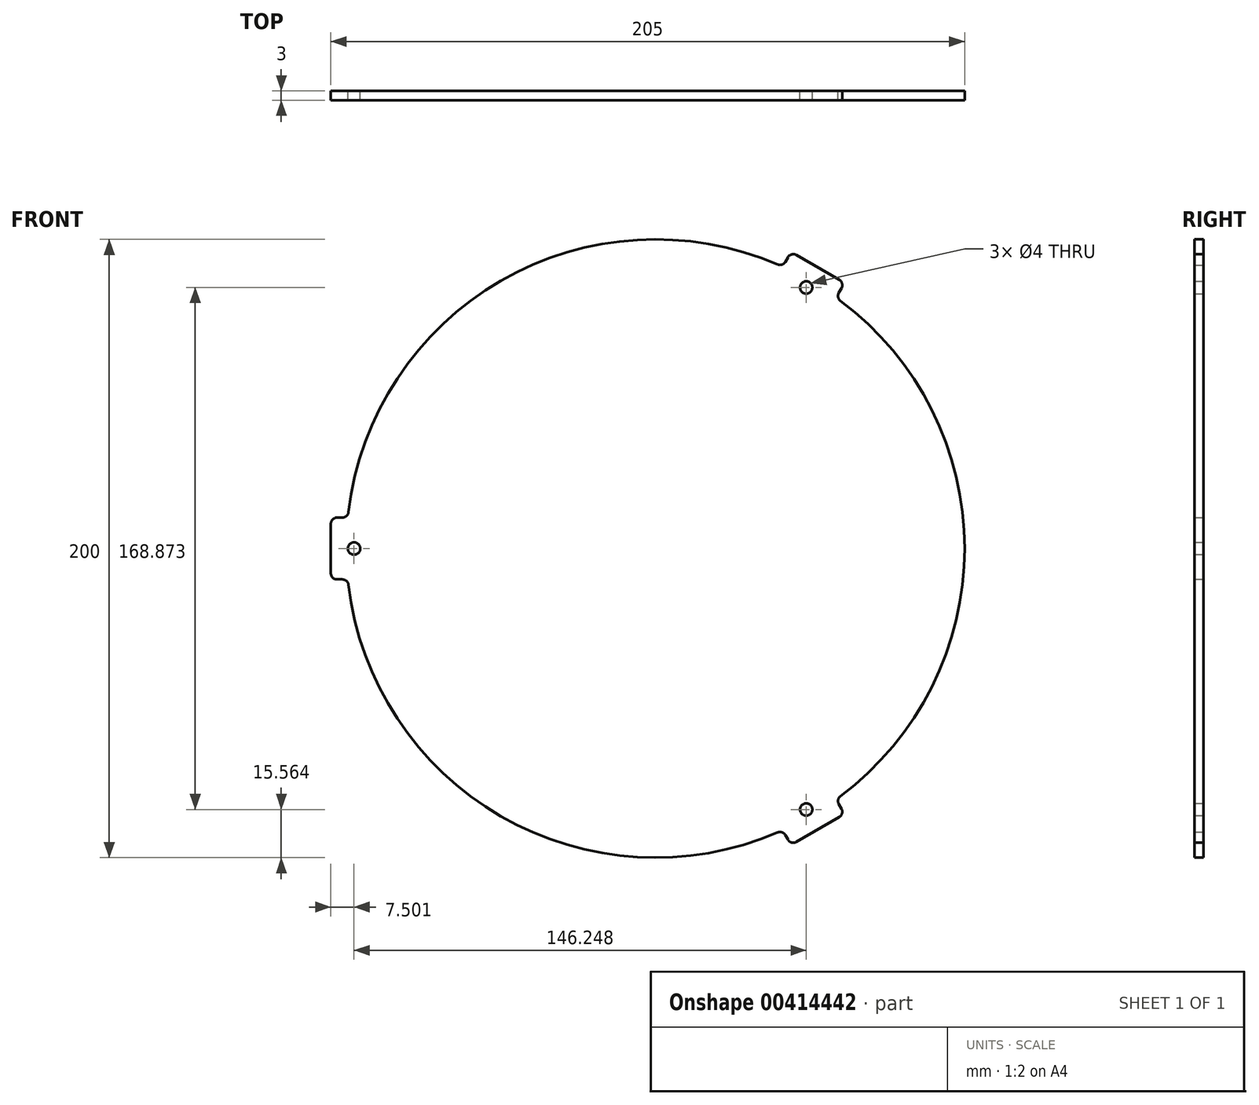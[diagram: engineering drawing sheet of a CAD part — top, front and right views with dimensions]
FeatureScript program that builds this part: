
annotation { "Feature Type Name" : "Feature", "Feature Type Description" : "" }
export const myFeature = defineFeature(function(context is Context, id is Id, definition is map)
    precondition{}
    {
        {
            var Q0;
            Q0=qCreatedBy(makeId("Front.planeOp"),FACE);
            var sketch = newSketch(context, id + "F0", { "sketchPlane" : qUnion([Q0])});
            skArc(sketch, "E0", {"start": v(-99.5, -10) * mm, "mid": v(-50, -86.6) * mm, "end": v(41.09, -91.17) * mm});
            skLineSegment(sketch, "E1", {"start": v(0, 0) * mm, "end": v(63.3, 109.65) * mm, "construction": true});
            skLineSegment(sketch, "E2", {"start": v(0, 0) * mm, "end": v(70.88, -122.77) * mm, "construction": true});
            skLineSegment(sketch, "E3", {"start": v(0, 0) * mm, "end": v(-175.52, 0) * mm, "construction": true});
            skCircle(sketch, "E4", {"center": v(0, 0) * mm, "radius": 105 * mm, "construction": true});
            skArc(sketch, "E5.trimOffspring", {"start": v(58.4, -81.17) * mm, "mid": v(100, 0) * mm, "end": v(58.4, 81.17) * mm});
            skArc(sketch, "E6.trimOffspring", {"start": v(41.09, 91.17) * mm, "mid": v(-50, 86.6) * mm, "end": v(-99.5, 10) * mm});
            skLineSegment(sketch, "E7", {"start": v(-105, 10) * mm, "end": v(-105, -10) * mm});
            skLineSegment(sketch, "E8", {"start": v(-105, 10) * mm, "end": v(-99.5, 10) * mm});
            skLineSegment(sketch, "E9.MirrorCS", {"start": v(-105, -10) * mm, "end": v(-99.5, -10) * mm});
            skLineSegment(sketch, "E10.1.0", {"start": v(43.84, -95.93) * mm, "end": v(41.09, -91.17) * mm});
            skLineSegment(sketch, "E10.1.1", {"start": v(43.84, -95.93) * mm, "end": v(61.16, -85.93) * mm});
            skLineSegment(sketch, "E10.1.2", {"start": v(61.16, -85.93) * mm, "end": v(58.4, -81.17) * mm});
            skLineSegment(sketch, "E10.2.0", {"start": v(61.16, 85.93) * mm, "end": v(58.4, 81.17) * mm});
            skLineSegment(sketch, "E10.2.1", {"start": v(61.16, 85.93) * mm, "end": v(43.84, 95.93) * mm});
            skLineSegment(sketch, "E10.2.2", {"start": v(43.84, 95.93) * mm, "end": v(41.09, 91.17) * mm});
            skCircle(sketch, "E11", {"center": v(-97.5, 0) * mm, "radius": 2 * mm});
            skCircle(sketch, "E12.1.0", {"center": v(48.75, -84.44) * mm, "radius": 2 * mm});
            skCircle(sketch, "E12.2.0", {"center": v(48.75, 84.44) * mm, "radius": 2 * mm});
            skCircle(sketch, "E13", {"center": v(0, 0) * mm, "radius": 97.5 * mm, "construction": true});
            skLineSegment(sketch, "E14", {"start": v(-99.5, 10) * mm, "end": v(-99.5, -10) * mm, "construction": true});
            skSolve(sketch);
        }
        {
            var Q0;
            Q0=qSketchRegion(id+"F0",true);
            extrude(context, id + "F1", {"entities" : qUnion([Q0]), "depth" : 3 * mm});
        }
        {
            var Q0;
            Q0=makeQuery(id+"F1.opExtrude","SWEPT_EDGE",EDGE,{"disambiguationData":[OSD([sQuery(id+"F0.wireOp",EDGE,"E5.trimOffspring"),sQuery(id+"F0.wireOp",EDGE,"E10.2.0")])]});
            var Q1;
            Q1=makeQuery(id+"F1.opExtrude","SWEPT_EDGE",EDGE,{"disambiguationData":[OSD([sQuery(id+"F0.wireOp",EDGE,"E6.trimOffspring"),sQuery(id+"F0.wireOp",EDGE,"E10.2.2")])]});
            var Q2;
            Q2=makeQuery(id+"F1.opExtrude","SWEPT_EDGE",EDGE,{"disambiguationData":[OSD([sQuery(id+"F0.wireOp",EDGE,"E5.trimOffspring"),sQuery(id+"F0.wireOp",EDGE,"E10.1.2")])]});
            var Q3;
            Q3=makeQuery(id+"F1.opExtrude","SWEPT_EDGE",EDGE,{"disambiguationData":[OSD([sQuery(id+"F0.wireOp",EDGE,"E0"),sQuery(id+"F0.wireOp",EDGE,"E10.1.0")])]});
            var Q4;
            Q4=makeQuery(id+"F1.opExtrude","SWEPT_EDGE",EDGE,{"disambiguationData":[OSD([sQuery(id+"F0.wireOp",EDGE,"E0"),sQuery(id+"F0.wireOp",EDGE,"E9.MirrorCS")])]});
            var Q5;
            Q5=makeQuery(id+"F1.opExtrude","SWEPT_EDGE",EDGE,{"disambiguationData":[OSD([sQuery(id+"F0.wireOp",EDGE,"E6.trimOffspring"),sQuery(id+"F0.wireOp",EDGE,"E8")])]});
            fillet(context, id + "F2", {"entities" : qUnion([Q0, Q1, Q2, Q3, Q4, Q5]), "radius" : 2 * mm, "tangentPropagation" : true, "allowEdgeOverflow" : false});
        }
        {
            var Q0;
            Q0=makeQuery(id+"F1.opExtrude","SWEPT_EDGE",EDGE,{"disambiguationData":[OSD([sQuery(id+"F0.wireOp",EDGE,"E10.2.0"),sQuery(id+"F0.wireOp",EDGE,"E10.2.1")])]});
            var Q1;
            Q1=makeQuery(id+"F1.opExtrude","SWEPT_EDGE",EDGE,{"disambiguationData":[OSD([sQuery(id+"F0.wireOp",EDGE,"E10.2.1"),sQuery(id+"F0.wireOp",EDGE,"E10.2.2")])]});
            var Q2;
            Q2=makeQuery(id+"F1.opExtrude","SWEPT_EDGE",EDGE,{"disambiguationData":[OSD([sQuery(id+"F0.wireOp",EDGE,"E7"),sQuery(id+"F0.wireOp",EDGE,"E8")])]});
            var Q3;
            Q3=makeQuery(id+"F1.opExtrude","SWEPT_EDGE",EDGE,{"disambiguationData":[OSD([sQuery(id+"F0.wireOp",EDGE,"E7"),sQuery(id+"F0.wireOp",EDGE,"E9.MirrorCS")])]});
            var Q4;
            Q4=makeQuery(id+"F1.opExtrude","SWEPT_EDGE",EDGE,{"disambiguationData":[OSD([sQuery(id+"F0.wireOp",EDGE,"E10.1.0"),sQuery(id+"F0.wireOp",EDGE,"E10.1.1")])]});
            var Q5;
            Q5=makeQuery(id+"F1.opExtrude","SWEPT_EDGE",EDGE,{"disambiguationData":[OSD([sQuery(id+"F0.wireOp",EDGE,"E10.1.1"),sQuery(id+"F0.wireOp",EDGE,"E10.1.2")])]});
            fillet(context, id + "F3", {"entities" : qUnion([Q0, Q1, Q2, Q3, Q4, Q5]), "radius" : 2 * mm, "tangentPropagation" : true, "allowEdgeOverflow" : false});
        }
    });
